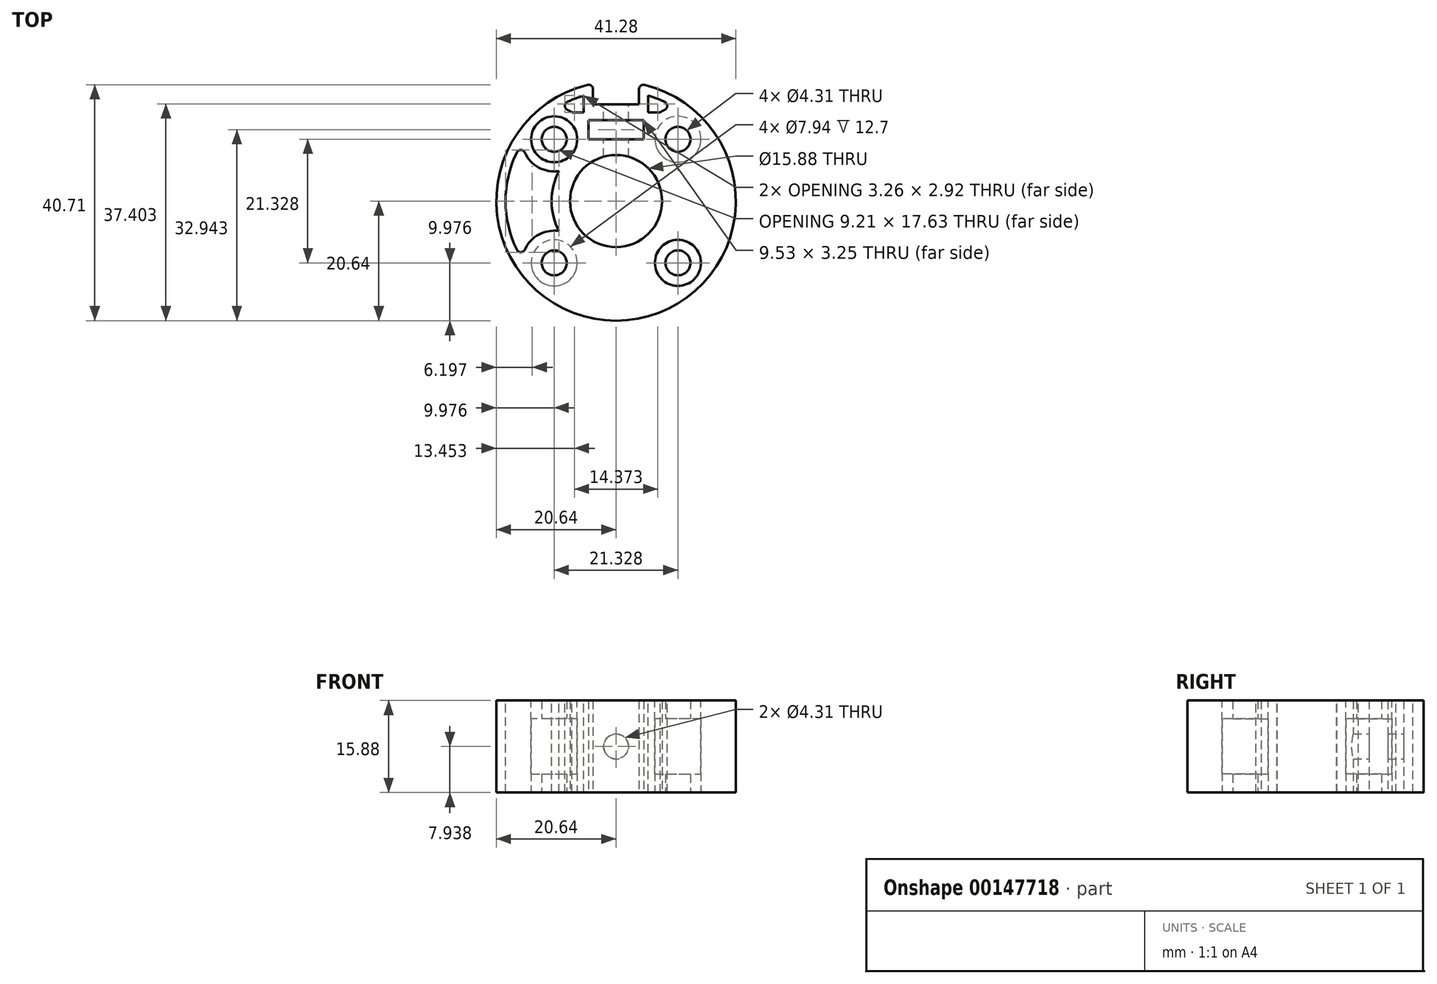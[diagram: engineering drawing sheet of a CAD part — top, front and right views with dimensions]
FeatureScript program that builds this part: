
annotation { "Feature Type Name" : "Feature", "Feature Type Description" : "" }
export const myFeature = defineFeature(function(context is Context, id is Id, definition is map)
    precondition{}
    {
        {
            var Q0;
            Q0=qCreatedBy(makeId("Top.planeOp"),FACE);
            var sketch = newSketch(context, id + "F0", { "sketchPlane" : qUnion([Q0])});
            skLineSegment(sketch, "E0.bottom", {"start": v(10.66, 10.66) * mm, "end": v(-10.66, 10.66) * mm, "construction": true});
            skLineSegment(sketch, "E0.top", {"start": v(10.66, -10.66) * mm, "end": v(-10.66, -10.66) * mm, "construction": true});
            skLineSegment(sketch, "E0.left", {"start": v(10.66, 10.66) * mm, "end": v(10.66, -10.66) * mm, "construction": true});
            skLineSegment(sketch, "E0.right", {"start": v(-10.66, 10.66) * mm, "end": v(-10.66, -10.66) * mm, "construction": true});
            skPoint(sketch, "E0.middle", {"position": v(0, 0) * mm});
            skCircle(sketch, "E1", {"center": v(-10.66, 10.66) * mm, "radius": 5.56 * mm, "construction": true});
            skLineSegment(sketch, "E2", {"start": v(0, 13.93) * mm, "end": v(0, 16.67) * mm});
            skLineSegment(sketch, "E3.bottom", {"start": v(-3.97, 20.25) * mm, "end": v(3.97, 20.25) * mm, "construction": true});
            skLineSegment(sketch, "E3.top", {"start": v(-3.97, 16.67) * mm, "end": v(3.97, 16.67) * mm});
            skLineSegment(sketch, "E3.left", {"start": v(-3.97, 20.25) * mm, "end": v(-3.97, 16.67) * mm});
            skLineSegment(sketch, "E3.right", {"start": v(3.97, 20.25) * mm, "end": v(3.97, 16.67) * mm});
            skArc(sketch, "E4", {"start": v(-3.97, 20.25) * mm, "mid": v(0, -20.64) * mm, "end": v(3.97, 20.25) * mm});
            skCircle(sketch, "E5", {"center": v(-10.66, 10.66) * mm, "radius": 2.15 * mm});
            skCircle(sketch, "E6", {"center": v(-10.66, -10.66) * mm, "radius": 2.15 * mm});
            skCircle(sketch, "E7", {"center": v(10.66, -10.66) * mm, "radius": 2.15 * mm});
            skCircle(sketch, "E8", {"center": v(10.66, 10.66) * mm, "radius": 2.15 * mm});
            skLineSegment(sketch, "E9.bottom", {"start": v(-4.76, 13.93) * mm, "end": v(4.76, 13.93) * mm});
            skLineSegment(sketch, "E9.top", {"start": v(-4.76, 10.68) * mm, "end": v(4.76, 10.68) * mm});
            skLineSegment(sketch, "E9.left", {"start": v(-4.76, 13.93) * mm, "end": v(-4.76, 10.68) * mm});
            skLineSegment(sketch, "E9.right", {"start": v(4.76, 13.93) * mm, "end": v(4.76, 10.68) * mm});
            skCircle(sketch, "E10", {"center": v(0, 0) * mm, "radius": 7.94 * mm});
            skCircle(sketch, "E11", {"center": v(0, 0) * mm, "radius": 9.53 * mm, "construction": true});
            skLineSegment(sketch, "E12", {"start": v(0, 0) * mm, "end": v(0, 7.14) * mm, "construction": true});
            skLineSegment(sketch, "E13", {"start": v(0, 7.14) * mm, "end": v(0, 7.94) * mm, "construction": true});
            skLineSegment(sketch, "E14", {"start": v(0, 7.94) * mm, "end": v(0, 10.68) * mm, "construction": true});
            skSolve(sketch);
        }
        {
            var Q0;
            Q0=qSketchRegion(id+"F0",true);
            extrude(context, id + "F1", {"entities" : qUnion([Q0]), "depth" : 15.88 * mm});
        }
        {
            var Q0;
            Q0=makeQuery(id+"F1.opExtrude","SWEPT_FACE",FACE,{"disambiguationData":[OSD([sQuery(id+"F0.wireOp",EDGE,"E3.top")])]});
            var sketch = newSketch(context, id + "F2", { "sketchPlane" : qUnion([Q0])});
            skLineSegment(sketch, "E15", {"start": v(0, 15.88) * mm, "end": v(0, 0) * mm, "construction": true});
            skCircle(sketch, "E16", {"center": v(0, 7.94) * mm, "radius": 2.15 * mm});
            skSolve(sketch);
        }
        {
            var Q0;
            Q0=qSketchRegion(id+"F2",true);
            var Q1;
            Q1=makeQuery(id+"F1.opExtrude","SWEPT_FACE",FACE,{"disambiguationData":[OSD([sQuery(id+"F0.wireOp",EDGE,"E10")])]});
            extrude(context, id + "F3", {"entities" : qUnion([Q0]), "operationType" : NewBodyOperationType.REMOVE, "endBound" : BoundingType.UP_TO_SURFACE, "oppositeDirection" : true, "endBoundEntityFace" : qUnion([Q1]), "depth" : 25.4 * mm});
        }
        {
            var Q0;
            Q0=makeQuery(id+"F1.opExtrude","CAP_FACE",FACE,{"disambiguationData":[OSD([sQuery(id+"F0.wireOp",EDGE,"zcYoioO2-fyPR-UuhC-Hgss-rbXFzuCLLck7"),sQuery(id+"F0.wireOp",EDGE,"E3.top"),sQuery(id+"F0.wireOp",EDGE,"E3.left"),sQuery(id+"F0.wireOp",EDGE,"E3.right"),sQuery(id+"F0.wireOp",EDGE,"E4"),sQuery(id+"F0.wireOp",EDGE,"E5"),sQuery(id+"F0.wireOp",EDGE,"E6"),sQuery(id+"F0.wireOp",EDGE,"E7"),sQuery(id+"F0.wireOp",EDGE,"E8")])],"isStart":true});
            cPlane(context, id + "F4", {"entities" : qUnion([Q0]), "cplaneType" : CPlaneType.OFFSET, "offset" : 3.17 * mm, "oppositeDirection" : true, "width" : 152.4 * mm, "height" : 152.4 * mm});
        }
        {
            var Q0;
            Q0=makeQuery(id+"F1.opExtrude","CAP_FACE",FACE,{"disambiguationData":[OSD([sQuery(id+"F0.wireOp",EDGE,"zcYoioO2-fyPR-UuhC-Hgss-rbXFzuCLLck7"),sQuery(id+"F0.wireOp",EDGE,"E3.top"),sQuery(id+"F0.wireOp",EDGE,"E3.left"),sQuery(id+"F0.wireOp",EDGE,"E3.right"),sQuery(id+"F0.wireOp",EDGE,"E4"),sQuery(id+"F0.wireOp",EDGE,"E5"),sQuery(id+"F0.wireOp",EDGE,"E6"),sQuery(id+"F0.wireOp",EDGE,"E7"),sQuery(id+"F0.wireOp",EDGE,"E8")])],"isStart":false});
            cPlane(context, id + "F5", {"entities" : qUnion([Q0]), "cplaneType" : CPlaneType.OFFSET, "offset" : 3.17 * mm, "oppositeDirection" : true, "width" : 152.4 * mm, "height" : 152.4 * mm});
        }
        {
            var Q0;
            Q0=makeQuery(id+"F1.opExtrude","CAP_FACE",FACE,{"disambiguationData":[OSD([sQuery(id+"F0.wireOp",EDGE,"zcYoioO2-fyPR-UuhC-Hgss-rbXFzuCLLck7"),sQuery(id+"F0.wireOp",EDGE,"E3.top"),sQuery(id+"F0.wireOp",EDGE,"E3.left"),sQuery(id+"F0.wireOp",EDGE,"E3.right"),sQuery(id+"F0.wireOp",EDGE,"E4"),sQuery(id+"F0.wireOp",EDGE,"E5"),sQuery(id+"F0.wireOp",EDGE,"E6"),sQuery(id+"F0.wireOp",EDGE,"E7"),sQuery(id+"F0.wireOp",EDGE,"E8")])],"isStart":false});
            var sketch = newSketch(context, id + "F6", { "sketchPlane" : qUnion([Q0])});
            skCircle(sketch, "E17", {"center": v(-10.66, 10.66) * mm, "radius": 3.97 * mm});
            skCircle(sketch, "E18", {"center": v(10.66, -10.66) * mm, "radius": 3.97 * mm});
            skSolve(sketch);
        }
        {
            var Q0;
            Q0=qSketchRegion(id+"F6",true);
            var Q1;
            Q1=qCreatedBy(id+"F4.planeOp",FACE);
            extrude(context, id + "F7", {"entities" : qUnion([Q0]), "operationType" : NewBodyOperationType.REMOVE, "endBound" : BoundingType.UP_TO_SURFACE, "oppositeDirection" : true, "endBoundEntityFace" : qUnion([Q1]), "depth" : 25.4 * mm});
        }
        {
            var Q0;
            Q0=makeQuery(id+"F1.opExtrude","CAP_FACE",FACE,{"disambiguationData":[OSD([sQuery(id+"F0.wireOp",EDGE,"zcYoioO2-fyPR-UuhC-Hgss-rbXFzuCLLck7"),sQuery(id+"F0.wireOp",EDGE,"E3.top"),sQuery(id+"F0.wireOp",EDGE,"E3.left"),sQuery(id+"F0.wireOp",EDGE,"E3.right"),sQuery(id+"F0.wireOp",EDGE,"E4"),sQuery(id+"F0.wireOp",EDGE,"E5"),sQuery(id+"F0.wireOp",EDGE,"E6"),sQuery(id+"F0.wireOp",EDGE,"E7"),sQuery(id+"F0.wireOp",EDGE,"E8")])],"isStart":true});
            var sketch = newSketch(context, id + "F8", { "sketchPlane" : qUnion([Q0])});
            skCircle(sketch, "E19", {"center": v(10.66, -10.66) * mm, "radius": 3.97 * mm});
            skCircle(sketch, "E20", {"center": v(-10.66, 10.66) * mm, "radius": 3.97 * mm});
            skSolve(sketch);
        }
        {
            var Q0;
            Q0=qSketchRegion(id+"F8",true);
            var Q1;
            Q1=qCreatedBy(id+"F5.planeOp",FACE);
            extrude(context, id + "F9", {"entities" : qUnion([Q0]), "operationType" : NewBodyOperationType.REMOVE, "endBound" : BoundingType.UP_TO_SURFACE, "oppositeDirection" : true, "endBoundEntityFace" : qUnion([Q1]), "depth" : 25.4 * mm});
        }
        {
            var Q0;
            Q0=makeQuery(id+"F1.opExtrude","CAP_FACE",FACE,{"disambiguationData":[OSD([sQuery(id+"F0.wireOp",EDGE,"zcYoioO2-fyPR-UuhC-Hgss-rbXFzuCLLck7"),sQuery(id+"F0.wireOp",EDGE,"E3.top"),sQuery(id+"F0.wireOp",EDGE,"E3.left"),sQuery(id+"F0.wireOp",EDGE,"E3.right"),sQuery(id+"F0.wireOp",EDGE,"E4"),sQuery(id+"F0.wireOp",EDGE,"E5"),sQuery(id+"F0.wireOp",EDGE,"E6"),sQuery(id+"F0.wireOp",EDGE,"E7"),sQuery(id+"F0.wireOp",EDGE,"E8")])],"isStart":false});
            var sketch = newSketch(context, id + "F10", { "sketchPlane" : qUnion([Q0])});
            skArc(sketch, "E21", {"start": v(-16.19, 10.05) * mm, "mid": v(-14.05, 6.26) * mm, "end": v(-9.84, 5.17) * mm});
            skArc(sketch, "E22", {"start": v(-16.19, 10.05) * mm, "mid": v(-19.05, 0) * mm, "end": v(-16.19, -10.05) * mm});
            skArc(sketch, "E23", {"start": v(-9.84, -5.17) * mm, "mid": v(-14.05, -6.26) * mm, "end": v(-16.19, -10.05) * mm});
            skArc(sketch, "E24", {"start": v(-9.84, 5.17) * mm, "mid": v(-11.11, 0) * mm, "end": v(-9.84, -5.17) * mm});
            skSolve(sketch);
        }
        {
            var Q0;
            Q0=qSketchRegion(id+"F10",true);
            var Q1;
            Q1=makeQuery(id+"F1.opExtrude","CAP_FACE",FACE,{"disambiguationData":[OSD([sQuery(id+"F0.wireOp",EDGE,"zcYoioO2-fyPR-UuhC-Hgss-rbXFzuCLLck7"),sQuery(id+"F0.wireOp",EDGE,"E3.top"),sQuery(id+"F0.wireOp",EDGE,"E3.left"),sQuery(id+"F0.wireOp",EDGE,"E3.right"),sQuery(id+"F0.wireOp",EDGE,"E4"),sQuery(id+"F0.wireOp",EDGE,"E5"),sQuery(id+"F0.wireOp",EDGE,"E6"),sQuery(id+"F0.wireOp",EDGE,"E7"),sQuery(id+"F0.wireOp",EDGE,"E8")])],"isStart":true});
            extrude(context, id + "F11", {"entities" : qUnion([Q0]), "operationType" : NewBodyOperationType.REMOVE, "endBound" : BoundingType.UP_TO_SURFACE, "oppositeDirection" : true, "endBoundEntityFace" : qUnion([Q1]), "depth" : 25.4 * mm});
        }
        {
            var Q0;
            Q0=makeQuery(id+"F1.opExtrude","SWEPT_FACE",FACE,{"disambiguationData":[OSD([sQuery(id+"F0.wireOp",EDGE,"E3.top")])]});
            var sketch = newSketch(context, id + "F12", { "sketchPlane" : qUnion([Q0])});
            skLineSegment(sketch, "E25", {"start": v(0, 0) * mm, "end": v(0, 15.88) * mm, "construction": true});
            skCircle(sketch, "E26", {"center": v(0, 7.94) * mm, "radius": 2.15 * mm});
            skSolve(sketch);
        }
        {
            var Q0;
            Q0=qSketchRegion(id+"F12",true);
            var Q1;
            Q1=makeQuery(id+"F1.opExtrude","SWEPT_FACE",FACE,{"disambiguationData":[OSD([sQuery(id+"F0.wireOp",EDGE,"E10")])]});
            extrude(context, id + "F13", {"entities" : qUnion([Q0]), "operationType" : NewBodyOperationType.REMOVE, "endBound" : BoundingType.UP_TO_SURFACE, "oppositeDirection" : true, "endBoundEntityFace" : qUnion([Q1]), "depth" : 25.4 * mm});
        }
        {
            var Q0;
            Q0=makeQuery(id+"F1.opExtrude","CAP_FACE",FACE,{"disambiguationData":[OSD([sQuery(id+"F0.wireOp",EDGE,"E3.top"),sQuery(id+"F0.wireOp",EDGE,"E3.left"),sQuery(id+"F0.wireOp",EDGE,"E3.right"),sQuery(id+"F0.wireOp",EDGE,"E4"),sQuery(id+"F0.wireOp",EDGE,"E5"),sQuery(id+"F0.wireOp",EDGE,"E6"),sQuery(id+"F0.wireOp",EDGE,"E7"),sQuery(id+"F0.wireOp",EDGE,"E8"),sQuery(id+"F0.wireOp",EDGE,"E9.bottom"),sQuery(id+"F0.wireOp",EDGE,"E9.top"),sQuery(id+"F0.wireOp",EDGE,"E9.left"),sQuery(id+"F0.wireOp",EDGE,"E9.right"),sQuery(id+"F0.wireOp",EDGE,"E10")])],"isStart":false});
            var sketch = newSketch(context, id + "F14", { "sketchPlane" : qUnion([Q0])});
            skArc(sketch, "E27", {"start": v(-7.6, 15.3) * mm, "mid": v(-8.77, 15.89) * mm, "end": v(-10.05, 16.19) * mm});
            skArc(sketch, "E28", {"start": v(-5.56, 18.22) * mm, "mid": v(-7.87, 17.35) * mm, "end": v(-10.05, 16.19) * mm});
            skLineSegment(sketch, "E29", {"start": v(-5.56, 18.22) * mm, "end": v(-5.56, 15.3) * mm});
            skLineSegment(sketch, "E30", {"start": v(-5.56, 15.3) * mm, "end": v(-7.6, 15.3) * mm});
            skCircle(sketch, "E31", {"center": v(-4.76, 13.93) * mm, "radius": 1.59 * mm, "construction": true});
            skLineSegment(sketch, "E32", {"start": v(5.56, 18.22) * mm, "end": v(5.56, 15.3) * mm});
            skLineSegment(sketch, "E33", {"start": v(5.56, 15.3) * mm, "end": v(7.6, 15.3) * mm});
            skArc(sketch, "E34", {"start": v(10.05, 16.19) * mm, "mid": v(7.87, 17.35) * mm, "end": v(5.56, 18.22) * mm});
            skArc(sketch, "E35", {"start": v(10.05, 16.19) * mm, "mid": v(8.77, 15.89) * mm, "end": v(7.6, 15.3) * mm});
            skSolve(sketch);
        }
        {
            var Q0;
            Q0=qSketchRegion(id+"F14",true);
            var Q1;
            Q1=makeQuery(id+"F1.opExtrude","CAP_FACE",FACE,{"disambiguationData":[OSD([sQuery(id+"F0.wireOp",EDGE,"E3.top"),sQuery(id+"F0.wireOp",EDGE,"E3.left"),sQuery(id+"F0.wireOp",EDGE,"E3.right"),sQuery(id+"F0.wireOp",EDGE,"E4"),sQuery(id+"F0.wireOp",EDGE,"E5"),sQuery(id+"F0.wireOp",EDGE,"E6"),sQuery(id+"F0.wireOp",EDGE,"E7"),sQuery(id+"F0.wireOp",EDGE,"E8"),sQuery(id+"F0.wireOp",EDGE,"E9.bottom"),sQuery(id+"F0.wireOp",EDGE,"E9.top"),sQuery(id+"F0.wireOp",EDGE,"E9.left"),sQuery(id+"F0.wireOp",EDGE,"E9.right"),sQuery(id+"F0.wireOp",EDGE,"E10")])],"isStart":true});
            extrude(context, id + "F15", {"entities" : qUnion([Q0]), "operationType" : NewBodyOperationType.REMOVE, "endBound" : BoundingType.UP_TO_SURFACE, "oppositeDirection" : true, "endBoundEntityFace" : qUnion([Q1]), "depth" : 25.4 * mm});
        }
        {
            var Q0;
            Q0=makeQuery(id+"F11.boolean.opBoolean","COPY",EDGE,{"derivedFrom":makeQuery(id+"F11.opExtrude","SWEPT_EDGE",EDGE,{"disambiguationData":[OSD([sQuery(id+"F10.wireOp",EDGE,"E22"),sQuery(id+"F10.wireOp",EDGE,"E23")])]})});
            var Q1;
            Q1=makeQuery(id+"FlX28BifZiOdl7F_1.1.F11.boolean.opBoolean","COPY",EDGE,{"derivedFrom":makeQuery(id+"FlX28BifZiOdl7F_1.1.F11.opExtrude","SWEPT_EDGE",EDGE,{"disambiguationData":[OSD([sQuery(id+"F10.wireOp",EDGE,"E21"),sQuery(id+"F10.wireOp",EDGE,"E22")])]})});
            var Q2;
            Q2=makeQuery(id+"F11.boolean.opBoolean","COPY",EDGE,{"derivedFrom":makeQuery(id+"F11.opExtrude","SWEPT_EDGE",EDGE,{"disambiguationData":[OSD([sQuery(id+"F10.wireOp",EDGE,"E21"),sQuery(id+"F10.wireOp",EDGE,"E22")])]})});
            var Q3;
            Q3=makeQuery(id+"FlX28BifZiOdl7F_1.1.F11.boolean.opBoolean","COPY",EDGE,{"derivedFrom":makeQuery(id+"FlX28BifZiOdl7F_1.1.F11.opExtrude","SWEPT_EDGE",EDGE,{"disambiguationData":[OSD([sQuery(id+"F10.wireOp",EDGE,"E22"),sQuery(id+"F10.wireOp",EDGE,"E23")])]})});
            var Q4;
            Q4=makeQuery(id+"FlX28BifZiOdl7F_1.2.F11.boolean.opBoolean","COPY",EDGE,{"derivedFrom":makeQuery(id+"FlX28BifZiOdl7F_1.2.F11.opExtrude","SWEPT_EDGE",EDGE,{"disambiguationData":[OSD([sQuery(id+"F10.wireOp",EDGE,"E21"),sQuery(id+"F10.wireOp",EDGE,"E22")])]})});
            var Q5;
            Q5=makeQuery(id+"FlX28BifZiOdl7F_1.2.F11.boolean.opBoolean","COPY",EDGE,{"derivedFrom":makeQuery(id+"FlX28BifZiOdl7F_1.2.F11.opExtrude","SWEPT_EDGE",EDGE,{"disambiguationData":[OSD([sQuery(id+"F10.wireOp",EDGE,"E22"),sQuery(id+"F10.wireOp",EDGE,"E23")])]})});
            var Q6;
            Q6=makeQuery(id+"F15.boolean.opBoolean","COPY",EDGE,{"derivedFrom":makeQuery(id+"F15.opExtrude","SWEPT_EDGE",EDGE,{"disambiguationData":[OSD([sQuery(id+"F14.wireOp",EDGE,"E34"),sQuery(id+"F14.wireOp",EDGE,"E35")])]})});
            var Q7;
            Q7=makeQuery(id+"F1.opExtrude","SWEPT_EDGE",EDGE,{"disambiguationData":[OSD([sQuery(id+"F0.wireOp",EDGE,"E3.right"),sQuery(id+"F0.wireOp",EDGE,"E4")])]});
            var Q8;
            Q8=makeQuery(id+"F1.opExtrude","SWEPT_EDGE",EDGE,{"disambiguationData":[OSD([sQuery(id+"F0.wireOp",EDGE,"E3.left"),sQuery(id+"F0.wireOp",EDGE,"E4")])]});
            var Q9;
            Q9=makeQuery(id+"F15.boolean.opBoolean","COPY",EDGE,{"derivedFrom":makeQuery(id+"F15.opExtrude","SWEPT_EDGE",EDGE,{"disambiguationData":[OSD([sQuery(id+"F14.wireOp",EDGE,"E27"),sQuery(id+"F14.wireOp",EDGE,"E28")])]})});
            fillet(context, id + "F16", {"entities" : qUnion([Q0, Q1, Q2, Q3, Q4, Q5, Q6, Q7, Q8, Q9]), "radius" : 0.76 * mm, "tangentPropagation" : true, "allowEdgeOverflow" : false});
        }
    });
